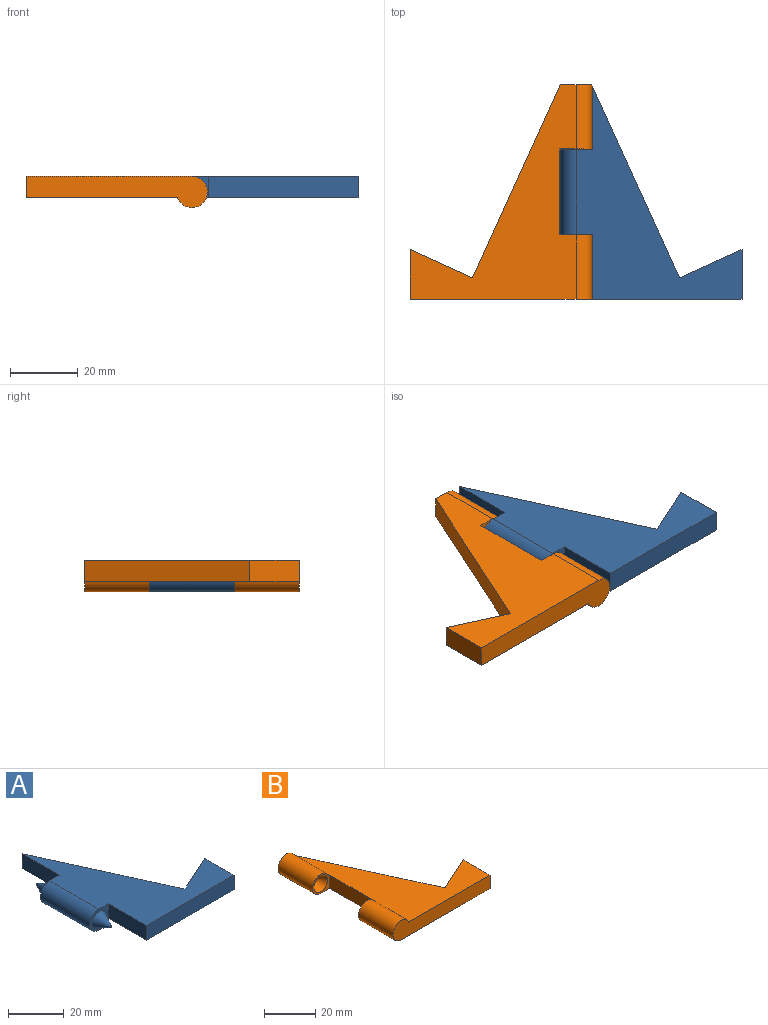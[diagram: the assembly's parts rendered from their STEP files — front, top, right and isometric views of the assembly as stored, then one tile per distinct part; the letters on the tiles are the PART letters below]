
ASSEMBLY  parts=2 mates=1
PART A: 15 faces, bbox 53.7x62.9x9.2 mm
  f0: plane 44.2x6.35mm, normal (0,-1,0), area 280.6mm2, adj f1,f2,f4,f14
  f1: plane 62.94x49.05mm, normal (0,0,1), area 1206.8mm2, adj f0,f3,f4,f5,f6,f7,f8,f13
  f2: plane 62.94x44.79mm, normal (0,0,-1), area 1100.7mm2, adj f0,f3,f4,f5,f6,f7,f8,f13
  f3: cylinder r=4.6mm len=24.89mm, axis (0,-1,0), area 495.4mm2, adj f1,f2,f7,f8
  f4: plane 14.75x6.35mm, normal (1,0,0), area 93.6mm2, adj f0,f1,f2,f5
  f5: plane 18.48x8.4mm, normal (-0.41,0.91,0), area 128.9mm2, adj f1,f2,f4,f6
  f6: plane 56.59x25.71mm, normal (0.91,0.41,0), area 394.7mm2, adj f1,f2,f5,f13
  f7: plane 9.46x9.21mm, normal (0,1,0), area 36mm2, adj f1,f2,f3,f12,f13
  f8: plane 9.46x9.21mm, normal (0,-1,0), area 36mm2, adj f1,f2,f3,f10,f14
  f9: plane 0.76x0.76mm, normal (0,-1,0), area 0.5mm2, adj f10
  f10: cone r=0.25mm half-angle=26.6deg, axis (0,1,0), area 81.6mm2, adj f8,f9
  f11: plane 0.76x0.76mm, normal (0,1,0), area 0.5mm2, adj f12
  f12: cone r=0.25mm half-angle=26.6deg, axis (0,-1,0), area 81.6mm2, adj f7,f11
  f13: plane 18.75x6.35mm, normal (-1,0,0), area 119mm2, adj f1,f2,f6,f7
  f14: plane 19.3x6.35mm, normal (-1,0,0), area 122.6mm2, adj f0,f1,f2,f8
PART B: 16 faces, bbox 53.7x63.5x9.2 mm
  f0: plane 63.5x44.79mm, normal (0,0,1), area 1108.6mm2, adj f2,f3,f4,f5,f6,f7,f8,f9
  f1: plane 63.5x49.05mm, normal (0,0,-1), area 1270.8mm2, adj f2,f3,f4,f5,f6,f7,f8,f9
  f2: cylinder r=4.6mm len=19.05mm, axis (0,-1,0), area 379.2mm2, adj f0,f1,f3,f9
  f3: plane 53.66x9.21mm, normal (0,-1,0), area 353.6mm2, adj f0,f1,f2,f4
  f4: plane 14.75x6.35mm, normal (1,0,0), area 93.6mm2, adj f0,f1,f3,f5
  f5: plane 18.48x8.4mm, normal (-0.41,0.91,0), area 128.9mm2, adj f0,f1,f4,f6
  f6: plane 57.15x25.97mm, normal (0.91,0.41,0), area 398.6mm2, adj f0,f1,f5,f8
  f7: cylinder r=4.6mm len=19.05mm, axis (0,-1,0), area 379.2mm2, adj f0,f1,f8,f10
  f8: plane 9.21x9.21mm, normal (0,1,0), area 71.3mm2, adj f0,f1,f6,f7
  f9: plane 9.46x9.21mm, normal (0,1,0), area 27.3mm2, adj f0,f1,f2,f14,f15
  f10: plane 9.46x9.21mm, normal (0,-1,0), area 27.3mm2, adj f0,f1,f7,f12,f15
  f11: plane 1.27x1.27mm, normal (0,-1,0), area 1.3mm2, adj f12
  f12: cone r=0.64mm half-angle=26.6deg, axis (0,-1,0), area 99.1mm2, adj f10,f11
  f13: plane 1.27x1.27mm, normal (0,1,0), area 1.3mm2, adj f14
  f14: cone r=0.64mm half-angle=26.6deg, axis (0,1,0), area 99.1mm2, adj f9,f13
  f15: plane 25.4x6.35mm, normal (-1,0,0), area 161.3mm2, adj f0,f1,f9,f10
PLACE A t=(-62.36,-34.42,-18.32)mm
PLACE B rot(axis=(0,1,0),180deg) t=(-71.57,-34.42,-11.97)mm
MATE planar A.f3 <-> B.f2  axis (0,1,0) through (-66.97,9.78,-16.57)mm
